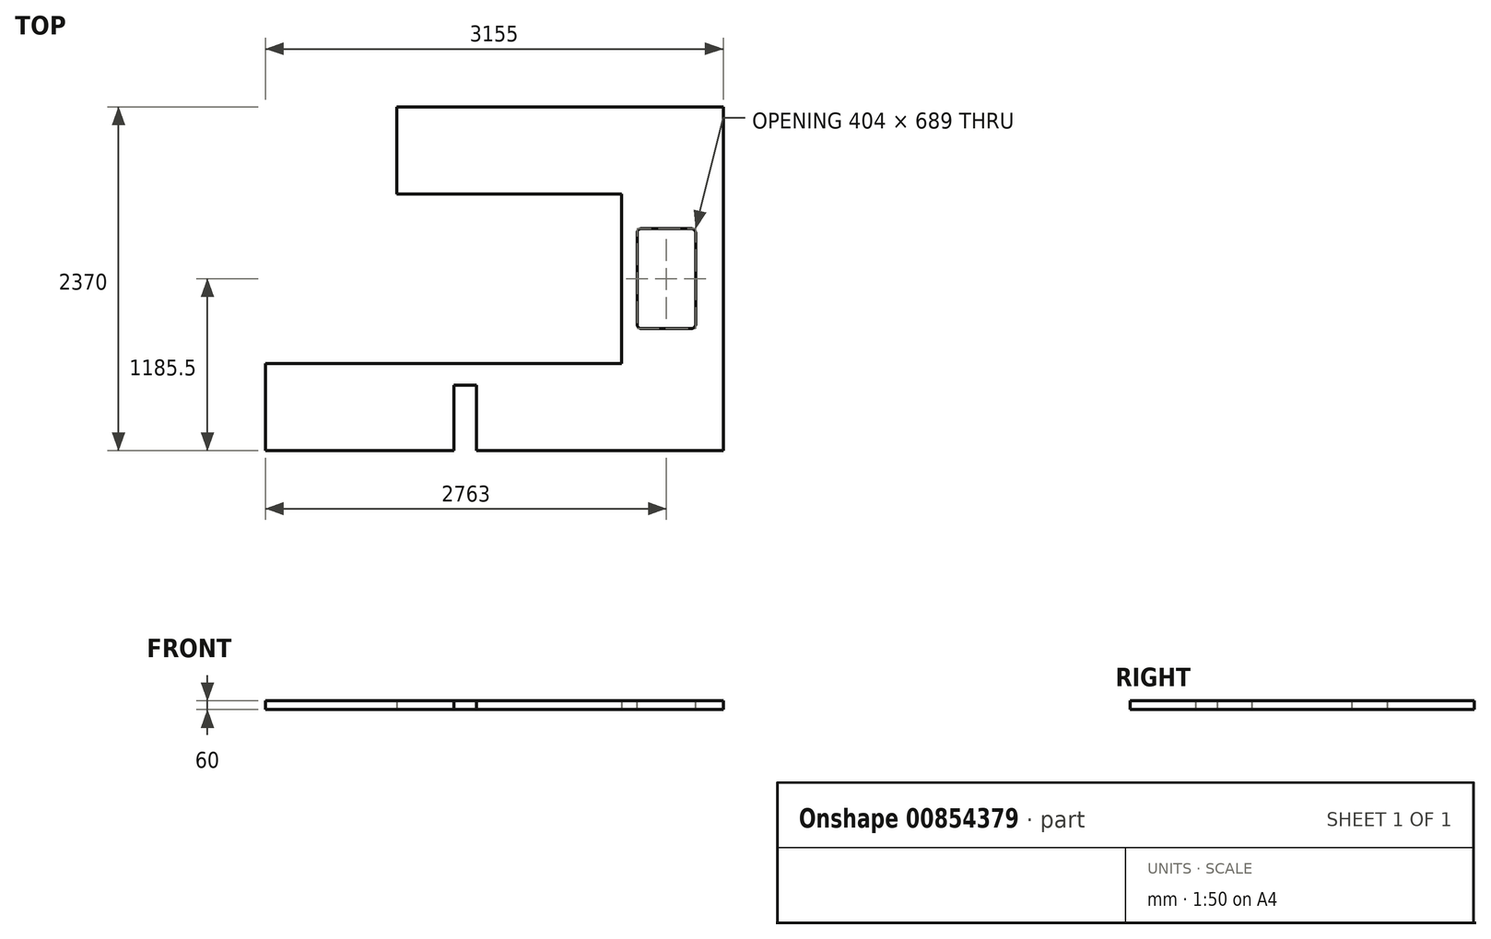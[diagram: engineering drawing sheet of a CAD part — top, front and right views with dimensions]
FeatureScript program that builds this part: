
annotation { "Feature Type Name" : "Feature", "Feature Type Description" : "" }
export const myFeature = defineFeature(function(context is Context, id is Id, definition is map)
    precondition{}
    {
        {
            var Q0;
            Q0=qCreatedBy(makeId("Top.planeOp"),FACE);
            var sketch = newSketch(context, id + "F0", { "sketchPlane" : qUnion([Q0])});
            skLineSegment(sketch, "E0", {"start": v(0, 0) * mm, "end": v(0, -450) * mm});
            skLineSegment(sketch, "E1", {"start": v(0, -450) * mm, "end": v(-1300, -450) * mm});
            skLineSegment(sketch, "E2", {"start": v(-1300, -450) * mm, "end": v(-1300, 150) * mm});
            skLineSegment(sketch, "E3", {"start": v(-1300, 150) * mm, "end": v(1155, 150) * mm});
            skLineSegment(sketch, "E4", {"start": v(1855, 1920) * mm, "end": v(1855, -450) * mm});
            skLineSegment(sketch, "E5", {"start": v(1855, -450) * mm, "end": v(155, -450) * mm});
            skLineSegment(sketch, "E6", {"start": v(155, -450) * mm, "end": v(155, 0) * mm});
            skLineSegment(sketch, "E7", {"start": v(155, 0) * mm, "end": v(0, 0) * mm});
            skLineSegment(sketch, "E8", {"start": v(1155, 150) * mm, "end": v(1155, 1320) * mm});
            skLineSegment(sketch, "E9", {"start": v(1155, 1320) * mm, "end": v(-395, 1320) * mm});
            skLineSegment(sketch, "E10", {"start": v(-395, 1320) * mm, "end": v(-395, 1920) * mm});
            skLineSegment(sketch, "E11", {"start": v(-395, 1920) * mm, "end": v(1855, 1920) * mm});
            skSolve(sketch);
        }
        {
            var Q0;
            Q0 = qSketchRegion(id + "F0", true);
            extrude(context, id + "F1", {"entities" : qUnion([Q0]), "depth" : 60 * mm, "offsetDistance" : 25 * mm});
        }
        {
            var Q0;
            Q0=makeQuery(id+"F1.opExtrude","CAP_FACE",FACE,{"disambiguationData":[OSD([sQuery(id+"F0.wireOp",EDGE,"E0"),sQuery(id+"F0.wireOp",EDGE,"E1"),sQuery(id+"F0.wireOp",EDGE,"E2"),sQuery(id+"F0.wireOp",EDGE,"E3"),sQuery(id+"F0.wireOp",EDGE,"E4"),sQuery(id+"F0.wireOp",EDGE,"E5"),sQuery(id+"F0.wireOp",EDGE,"E6"),sQuery(id+"F0.wireOp",EDGE,"E7"),sQuery(id+"F0.wireOp",EDGE,"E8"),sQuery(id+"F0.wireOp",EDGE,"E9"),sQuery(id+"F0.wireOp",EDGE,"E10"),sQuery(id+"F0.wireOp",EDGE,"E11")])],"isStart":false});
            var sketch = newSketch(context, id + "F2", { "sketchPlane" : qUnion([Q0])});
            skLineSegment(sketch, "E12.bottom", {"start": v(1635, 1080) * mm, "end": v(1291, 1080) * mm});
            skLineSegment(sketch, "E12.top", {"start": v(1635, 391) * mm, "end": v(1291, 391) * mm});
            skLineSegment(sketch, "E12.left", {"start": v(1665, 1050) * mm, "end": v(1665, 421) * mm});
            skLineSegment(sketch, "E12.right", {"start": v(1261, 1050) * mm, "end": v(1261, 421) * mm});
            skPoint(sketch, "E13.visualSharp", {"position": v(1665, 391) * mm});
            skArc(sketch, "E13.filletArc", {"start": v(1635, 391) * mm, "mid": v(1656.21, 399.79) * mm, "end": v(1665, 421) * mm});
            skPoint(sketch, "E14.visualSharp", {"position": v(1261, 391) * mm});
            skArc(sketch, "E14.filletArc", {"start": v(1261, 421) * mm, "mid": v(1269.79, 399.79) * mm, "end": v(1291, 391) * mm});
            skPoint(sketch, "E15.visualSharp", {"position": v(1261, 1080) * mm});
            skArc(sketch, "E15.filletArc", {"start": v(1291, 1080) * mm, "mid": v(1269.79, 1071.21) * mm, "end": v(1261, 1050) * mm});
            skPoint(sketch, "E16.visualSharp", {"position": v(1665, 1080) * mm});
            skArc(sketch, "E16.filletArc", {"start": v(1665, 1050) * mm, "mid": v(1656.21, 1071.21) * mm, "end": v(1635, 1080) * mm});
            skSolve(sketch);
        }
        {
            var Q0;
            Q0 = qSketchRegion(id + "F2", true);
            extrude(context, id + "F3", {"entities" : qUnion([Q0]), "operationType" : NewBodyOperationType.REMOVE, "endBound" : BoundingType.UP_TO_NEXT, "oppositeDirection" : true, "depth" : 25 * mm, "offsetDistance" : 25 * mm});
        }
    });
